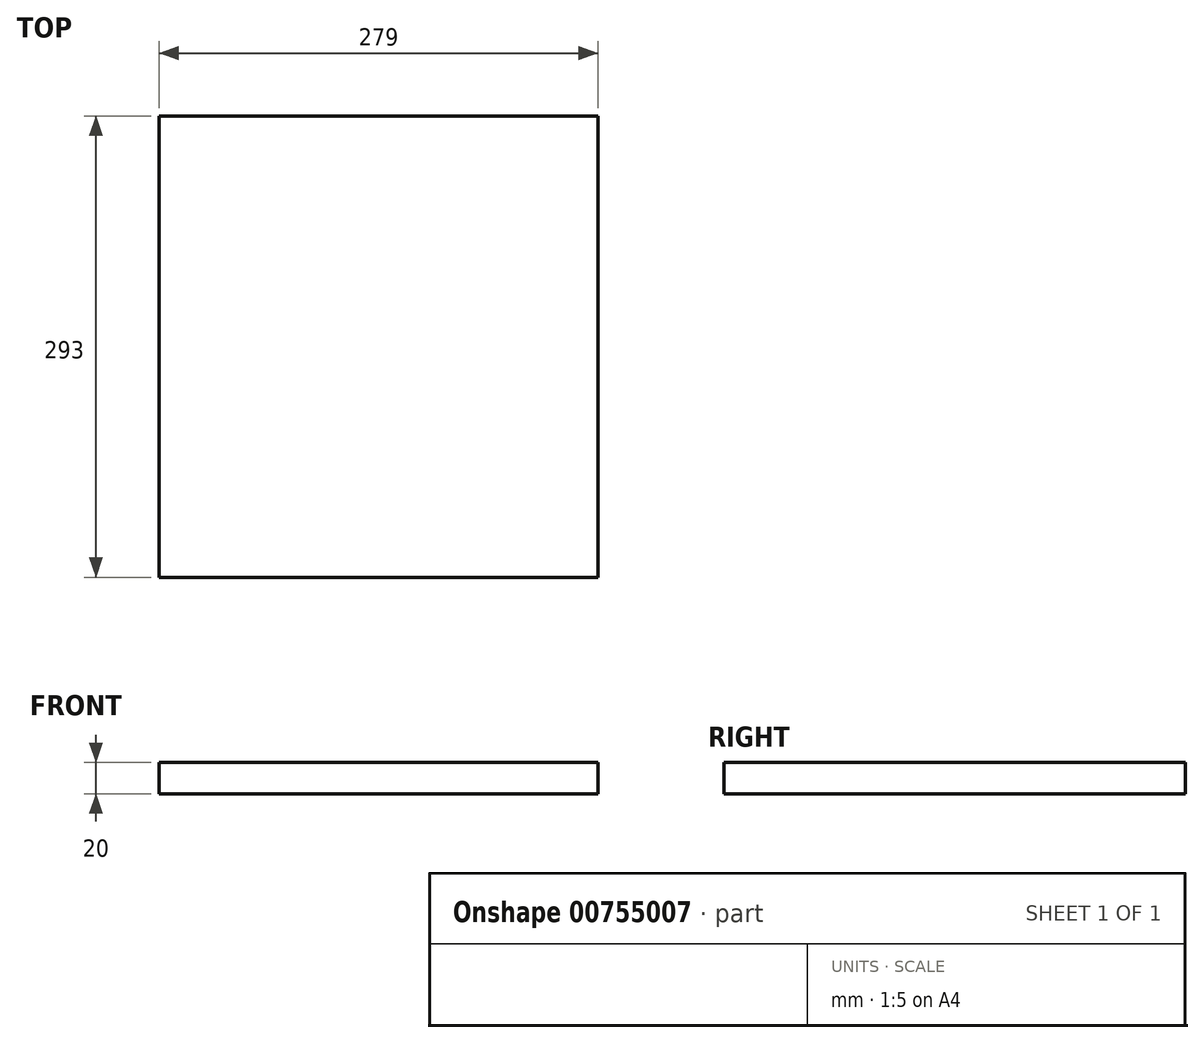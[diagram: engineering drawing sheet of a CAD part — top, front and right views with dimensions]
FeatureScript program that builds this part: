
annotation { "Feature Type Name" : "Feature", "Feature Type Description" : "" }
export const myFeature = defineFeature(function(context is Context, id is Id, definition is map)
    precondition{}
    {
        {
            var Q0;
            Q0=qCreatedBy(makeId("Top.planeOp"),FACE);
            var sketch = newSketch(context, id + "F0", { "sketchPlane" : qUnion([Q0])});
            skLineSegment(sketch, "E0.bottom", {"start": v(-376.57, 261.2) * mm, "end": v(-97.57, 261.2) * mm});
            skLineSegment(sketch, "E0.top", {"start": v(-376.57, -31.8) * mm, "end": v(-97.57, -31.8) * mm});
            skLineSegment(sketch, "E0.left", {"start": v(-376.57, 261.2) * mm, "end": v(-376.57, -31.8) * mm});
            skLineSegment(sketch, "E0.right", {"start": v(-97.57, 261.2) * mm, "end": v(-97.57, -31.8) * mm});
            skSolve(sketch);
        }
        {
            var Q0;
            Q0 = qSketchRegion(id + "F0", true);
            extrude(context, id + "F1", {"entities" : qUnion([Q0]), "depth" : 20 * mm, "offsetDistance" : 25 * mm});
        }
    });
